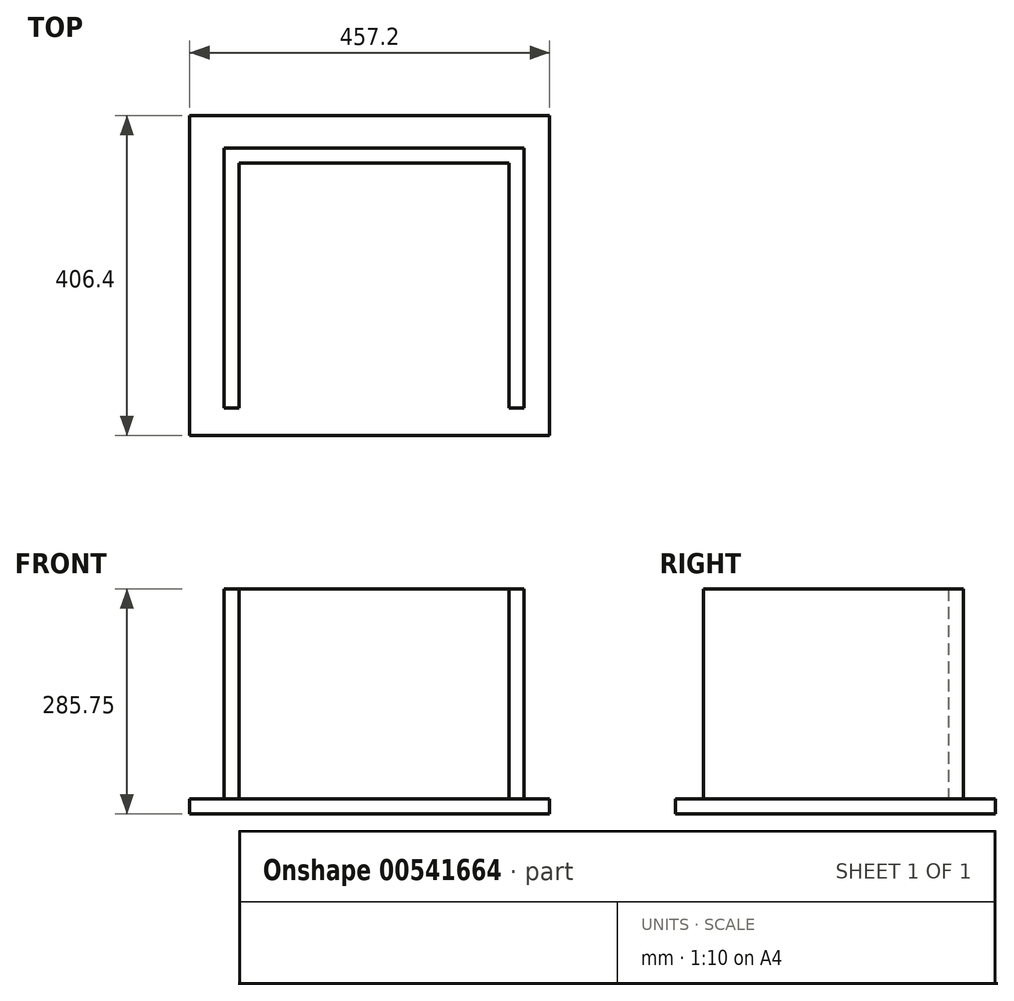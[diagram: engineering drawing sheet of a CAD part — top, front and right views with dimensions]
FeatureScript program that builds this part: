
annotation { "Feature Type Name" : "Feature", "Feature Type Description" : "" }
export const myFeature = defineFeature(function(context is Context, id is Id, definition is map)
    precondition{}
    {
        {
            var Q0;
            Q0=qCreatedBy(makeId("Top.planeOp"),FACE);
            var sketch = newSketch(context, id + "F0", { "sketchPlane" : qUnion([Q0])});
            skLineSegment(sketch, "E0.bottom", {"start": v(-228.6, 203.2) * mm, "end": v(228.6, 203.2) * mm});
            skLineSegment(sketch, "E0.top", {"start": v(-228.6, -203.2) * mm, "end": v(228.6, -203.2) * mm});
            skLineSegment(sketch, "E0.left", {"start": v(-228.6, 203.2) * mm, "end": v(-228.6, -203.2) * mm});
            skLineSegment(sketch, "E0.right", {"start": v(228.6, 203.2) * mm, "end": v(228.6, -203.2) * mm});
            skPoint(sketch, "E0.middle", {"position": v(0, 0) * mm});
            skSolve(sketch);
        }
        {
            var Q0;
            Q0 = qSketchRegion(id + "F0", true);
            extrude(context, id + "F1", {"entities" : qUnion([Q0]), "depth" : 19.05 * mm, "offsetDistance" : 25.4 * mm});
        }
        {
            var Q0;
            Q0=makeQuery(id+"F1.opExtrude","CAP_FACE",FACE,{"disambiguationData":[OSD([sQuery(id+"F0.wireOp",EDGE,"E0.bottom"),sQuery(id+"F0.wireOp",EDGE,"E0.top"),sQuery(id+"F0.wireOp",EDGE,"E0.left"),sQuery(id+"F0.wireOp",EDGE,"E0.right")])],"isStart":false});
            var sketch = newSketch(context, id + "F2", { "sketchPlane" : qUnion([Q0])});
            skLineSegment(sketch, "E1.bottom", {"start": v(-185.2, -168.12) * mm, "end": v(-166.15, -168.12) * mm});
            skLineSegment(sketch, "E1.top", {"start": v(-185.2, 162.08) * mm, "end": v(-166.15, 162.08) * mm});
            skLineSegment(sketch, "E1.left", {"start": v(-185.2, -168.12) * mm, "end": v(-185.2, 162.08) * mm});
            skLineSegment(sketch, "E1.right", {"start": v(-166.15, -168.12) * mm, "end": v(-166.15, 162.08) * mm});
            skLineSegment(sketch, "E2.bottom", {"start": v(195.8, -168.08) * mm, "end": v(176.75, -168.08) * mm});
            skLineSegment(sketch, "E2.top", {"start": v(195.8, 162.12) * mm, "end": v(176.75, 162.12) * mm});
            skLineSegment(sketch, "E2.left", {"start": v(195.8, -168.08) * mm, "end": v(195.8, 162.12) * mm});
            skLineSegment(sketch, "E2.right", {"start": v(176.75, -168.08) * mm, "end": v(176.75, 162.12) * mm});
            skLineSegment(sketch, "E3.bottom", {"start": v(-166.15, 162.08) * mm, "end": v(176.75, 162.08) * mm});
            skLineSegment(sketch, "E3.top", {"start": v(-166.15, 143.07) * mm, "end": v(176.75, 143.07) * mm});
            skLineSegment(sketch, "E3.left", {"start": v(-166.15, 162.08) * mm, "end": v(-166.15, 143.07) * mm});
            skLineSegment(sketch, "E3.right", {"start": v(176.75, 162.08) * mm, "end": v(176.75, 143.07) * mm});
            skSolve(sketch);
        }
        {
            var Q0;
            Q0 = qSketchRegion(id + "F2", true);
            extrude(context, id + "F3", {"entities" : qUnion([Q0]), "operationType" : NewBodyOperationType.ADD, "depth" : 266.7 * mm, "offsetDistance" : 25.4 * mm});
        }
    });
